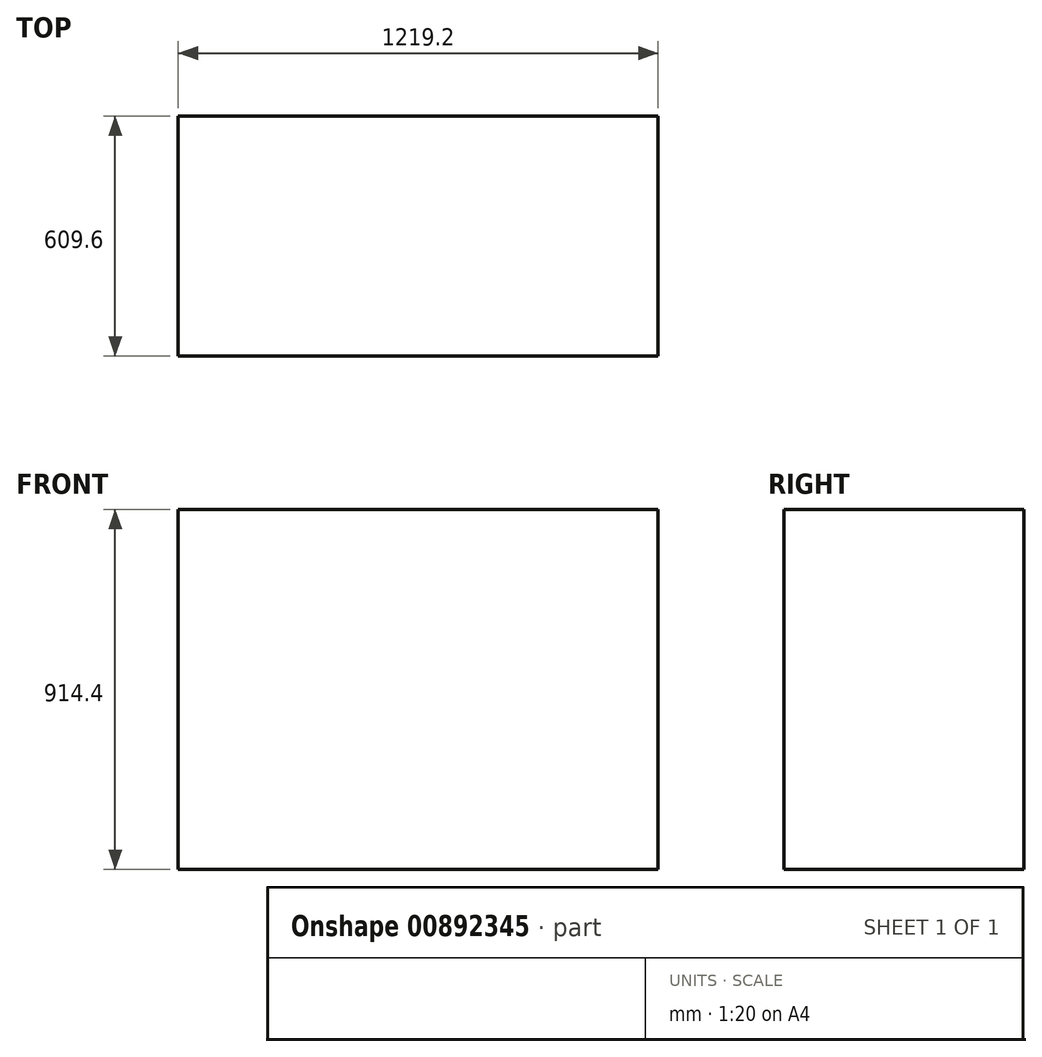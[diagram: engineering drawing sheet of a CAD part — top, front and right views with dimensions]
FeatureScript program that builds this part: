
annotation { "Feature Type Name" : "Feature", "Feature Type Description" : "" }
export const myFeature = defineFeature(function(context is Context, id is Id, definition is map)
    precondition{}
    {
        {
            var Q0;
            Q0=qCreatedBy(makeId("Top.planeOp"),FACE);
            var sketch = newSketch(context, id + "F0", { "sketchPlane" : qUnion([Q0])});
            skLineSegment(sketch, "E0.bottom", {"start": v(609.6, -304.8) * mm, "end": v(-609.6, -304.8) * mm});
            skLineSegment(sketch, "E0.top", {"start": v(609.6, 304.8) * mm, "end": v(-609.6, 304.8) * mm});
            skLineSegment(sketch, "E0.left", {"start": v(609.6, -304.8) * mm, "end": v(609.6, 304.8) * mm});
            skLineSegment(sketch, "E0.right", {"start": v(-609.6, -304.8) * mm, "end": v(-609.6, 304.8) * mm});
            skPoint(sketch, "E0.middle", {"position": v(0, 0) * mm});
            skSolve(sketch);
        }
        {
            var Q0;
            Q0 = qSketchRegion(id + "F0", true);
            extrude(context, id + "F1", {"entities" : qUnion([Q0]), "depth" : 914.4 * mm, "offsetDistance" : 25.4 * mm});
        }
    });
